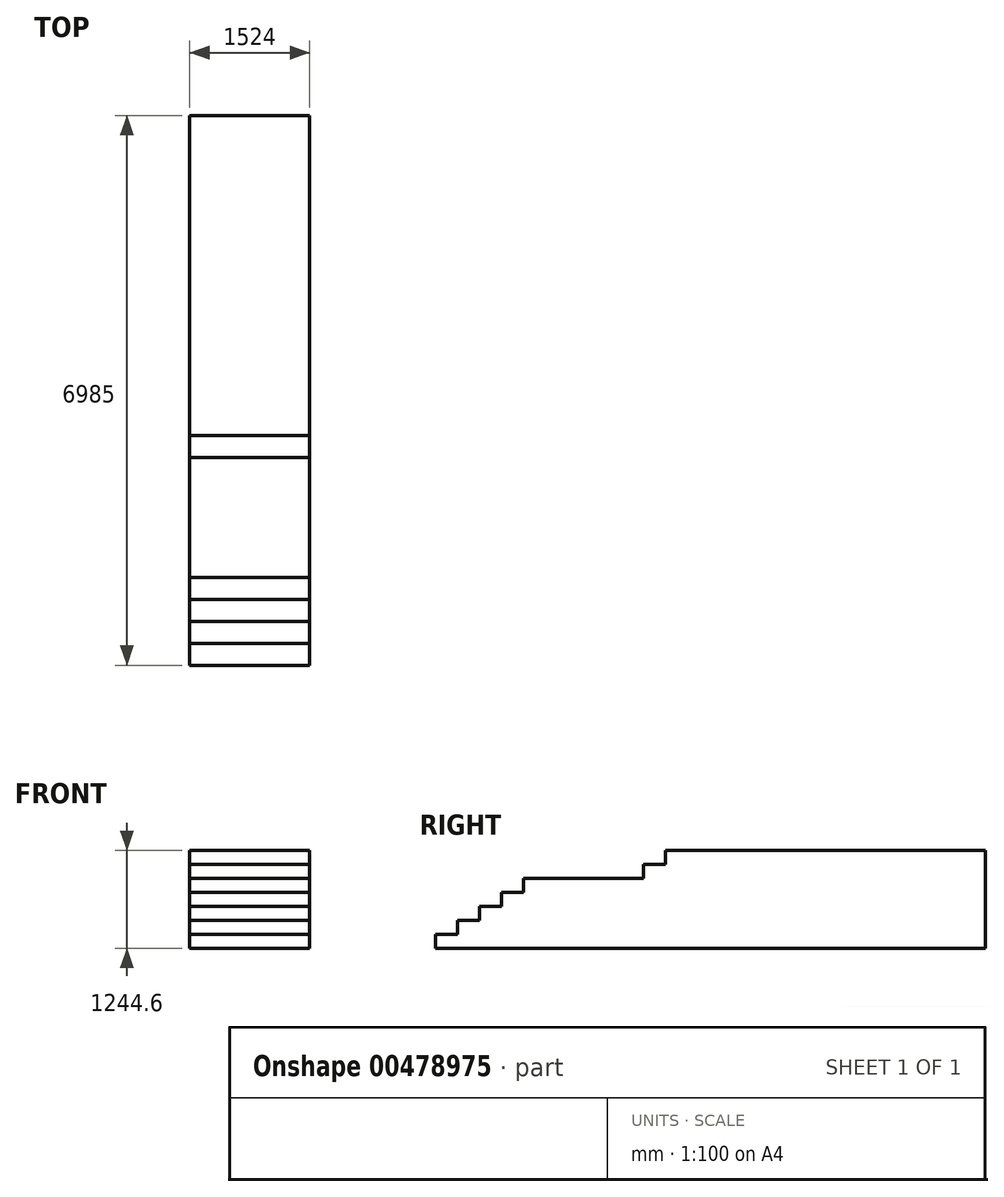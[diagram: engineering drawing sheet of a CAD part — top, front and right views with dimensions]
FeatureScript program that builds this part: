
annotation { "Feature Type Name" : "Feature", "Feature Type Description" : "" }
export const myFeature = defineFeature(function(context is Context, id is Id, definition is map)
    precondition{}
    {
        {
            var Q0;
            Q0=qCreatedBy(makeId("Top.planeOp"),FACE);
            var sketch = newSketch(context, id + "F0", { "sketchPlane" : qUnion([Q0])});
            skLineSegment(sketch, "E0.bottom", {"start": v(-763, 4345.35) * mm, "end": v(761, 4345.35) * mm});
            skLineSegment(sketch, "E0.top", {"start": v(-763, -2639.65) * mm, "end": v(761, -2639.65) * mm});
            skLineSegment(sketch, "E0.left", {"start": v(-763, 4345.35) * mm, "end": v(-763, -2639.65) * mm});
            skLineSegment(sketch, "E0.right", {"start": v(761, 4345.35) * mm, "end": v(761, -2639.65) * mm});
            skSolve(sketch);
        }
        {
            var Q0;
            Q0 = qSketchRegion(id + "F0", true);
            extrude(context, id + "F1", {"entities" : qUnion([Q0]), "depth" : 177.8 * mm});
        }
        {
            var Q0;
            Q0=makeQuery(id+"F1.opExtrude","CAP_FACE",FACE,{"disambiguationData":[OSD([sQuery(id+"F0.wireOp",EDGE,"E0.bottom"),sQuery(id+"F0.wireOp",EDGE,"E0.top"),sQuery(id+"F0.wireOp",EDGE,"E0.left"),sQuery(id+"F0.wireOp",EDGE,"E0.right")])],"isStart":false});
            var sketch = newSketch(context, id + "F2", { "sketchPlane" : qUnion([Q0])});
            skPoint(sketch, "E1", {"position": v(-763, -2360.25) * mm});
            skPoint(sketch, "E2", {"position": v(761, -2360.25) * mm});
            skLineSegment(sketch, "E3.bottom", {"start": v(-763, -2360.25) * mm, "end": v(761, -2360.25) * mm});
            skLineSegment(sketch, "E3.top", {"start": v(-763, 4345.35) * mm, "end": v(761, 4345.35) * mm});
            skLineSegment(sketch, "E3.left", {"start": v(-763, -2360.25) * mm, "end": v(-763, 4345.35) * mm});
            skLineSegment(sketch, "E3.right", {"start": v(761, -2360.25) * mm, "end": v(761, 4345.35) * mm});
            skSolve(sketch);
        }
        {
            var Q0;
            Q0=makeQuery(id+"F2.imprint","IMPRINT",FACE,{"disambiguationData":[TD([[makeQuery(id+"F2.imprint","IMPRINT",EDGE,{"derivedFrom":sQuery(id+"F2.wireOp",EDGE,"E3.bottom")}),1.0]])]});
            extrude(context, id + "F3", {"entities" : qUnion([Q0]), "operationType" : NewBodyOperationType.ADD, "depth" : 177.8 * mm});
        }
        {
            var Q0;
            Q0=makeQuery(id+"F3.opExtrude","CAP_FACE",FACE,{"disambiguationData":[OSD([sQuery(id+"F2.wireOp",EDGE,"E3.bottom"),sQuery(id+"F2.wireOp",EDGE,"E3.top"),sQuery(id+"F2.wireOp",EDGE,"E3.left"),sQuery(id+"F2.wireOp",EDGE,"E3.right")])],"isStart":false});
            var sketch = newSketch(context, id + "F4", { "sketchPlane" : qUnion([Q0])});
            skPoint(sketch, "E4", {"position": v(-763, -2080.85) * mm});
            skPoint(sketch, "E5", {"position": v(761, -2080.85) * mm});
            skLineSegment(sketch, "E6.bottom", {"start": v(-763, -2080.85) * mm, "end": v(761, -2080.85) * mm});
            skLineSegment(sketch, "E6.top", {"start": v(-763, 4345.35) * mm, "end": v(761, 4345.35) * mm});
            skLineSegment(sketch, "E6.left", {"start": v(-763, -2080.85) * mm, "end": v(-763, 4345.35) * mm});
            skLineSegment(sketch, "E6.right", {"start": v(761, -2080.85) * mm, "end": v(761, 4345.35) * mm});
            skSolve(sketch);
        }
        {
            var Q0;
            Q0 = qSketchRegion(id + "F4", true);
            var Q1;
            Q1=makeQuery(id+"F4.imprint","IMPRINT",FACE,{"disambiguationData":[TD([[makeQuery(id+"F4.imprint","IMPRINT",EDGE,{"derivedFrom":sQuery(id+"F4.wireOp",EDGE,"E6.bottom")}),1.0]])]});
            extrude(context, id + "F5", {"entities" : qUnion([Q0, Q1]), "operationType" : NewBodyOperationType.ADD, "depth" : 177.8 * mm});
        }
        {
            var Q0;
            Q0=makeQuery(id+"F5.opExtrude","CAP_FACE",FACE,{"disambiguationData":[OSD([sQuery(id+"F4.wireOp",EDGE,"E6.bottom"),sQuery(id+"F4.wireOp",EDGE,"E6.top"),sQuery(id+"F4.wireOp",EDGE,"E6.left"),sQuery(id+"F4.wireOp",EDGE,"E6.right")])],"isStart":false});
            var sketch = newSketch(context, id + "F6", { "sketchPlane" : qUnion([Q0])});
            skPoint(sketch, "E7", {"position": v(-763, -1801.45) * mm});
            skPoint(sketch, "E8", {"position": v(761, -1801.45) * mm});
            skLineSegment(sketch, "E9.bottom", {"start": v(-763, -1801.45) * mm, "end": v(761, -1801.45) * mm});
            skLineSegment(sketch, "E9.top", {"start": v(-763, 4345.35) * mm, "end": v(761, 4345.35) * mm});
            skLineSegment(sketch, "E9.left", {"start": v(-763, -1801.45) * mm, "end": v(-763, 4345.35) * mm});
            skLineSegment(sketch, "E9.right", {"start": v(761, -1801.45) * mm, "end": v(761, 4345.35) * mm});
            skSolve(sketch);
        }
        {
            var Q0;
            Q0 = qSketchRegion(id + "F6", true);
            extrude(context, id + "F7", {"entities" : qUnion([Q0]), "operationType" : NewBodyOperationType.ADD, "depth" : 177.8 * mm});
        }
        {
            var Q0;
            Q0=makeQuery(id+"F7.opExtrude","CAP_FACE",FACE,{"disambiguationData":[OSD([sQuery(id+"F6.wireOp",EDGE,"E9.bottom"),sQuery(id+"F6.wireOp",EDGE,"E9.top"),sQuery(id+"F6.wireOp",EDGE,"E9.left"),sQuery(id+"F6.wireOp",EDGE,"E9.right")])],"isStart":false});
            var sketch = newSketch(context, id + "F8", { "sketchPlane" : qUnion([Q0])});
            skPoint(sketch, "E10", {"position": v(-763, -1522.05) * mm});
            skPoint(sketch, "E11", {"position": v(761, -1522.05) * mm});
            skLineSegment(sketch, "E12.bottom", {"start": v(-763, -1522.05) * mm, "end": v(761, -1522.05) * mm});
            skLineSegment(sketch, "E12.top", {"start": v(-763, 4345.35) * mm, "end": v(761, 4345.35) * mm});
            skLineSegment(sketch, "E12.left", {"start": v(-763, -1522.05) * mm, "end": v(-763, 4345.35) * mm});
            skLineSegment(sketch, "E12.right", {"start": v(761, -1522.05) * mm, "end": v(761, 4345.35) * mm});
            skSolve(sketch);
        }
        {
            var Q0;
            Q0 = qSketchRegion(id + "F8", true);
            var Q1;
            Q1=makeQuery(id+"F8.imprint","IMPRINT",FACE,{"disambiguationData":[TD([[makeQuery(id+"F8.imprint","IMPRINT",EDGE,{"derivedFrom":sQuery(id+"F8.wireOp",EDGE,"E12.bottom")}),1.0]])]});
            extrude(context, id + "F9", {"entities" : qUnion([Q0, Q1]), "operationType" : NewBodyOperationType.ADD, "depth" : 177.8 * mm});
        }
        {
            var Q0;
            Q0=makeQuery(id+"F9.opExtrude","CAP_FACE",FACE,{"disambiguationData":[OSD([sQuery(id+"F8.wireOp",EDGE,"E12.bottom"),sQuery(id+"F8.wireOp",EDGE,"E12.top"),sQuery(id+"F8.wireOp",EDGE,"E12.left"),sQuery(id+"F8.wireOp",EDGE,"E12.right")])],"isStart":false});
            var sketch = newSketch(context, id + "F10", { "sketchPlane" : qUnion([Q0])});
            skPoint(sketch, "E13", {"position": v(-763, 1.95) * mm});
            skPoint(sketch, "E14", {"position": v(761, 1.95) * mm});
            skLineSegment(sketch, "E15.bottom", {"start": v(-763, 1.95) * mm, "end": v(761, 1.95) * mm});
            skLineSegment(sketch, "E15.top", {"start": v(-763, 4345.35) * mm, "end": v(761, 4345.35) * mm});
            skLineSegment(sketch, "E15.left", {"start": v(-763, 1.95) * mm, "end": v(-763, 4345.35) * mm});
            skLineSegment(sketch, "E15.right", {"start": v(761, 1.95) * mm, "end": v(761, 4345.35) * mm});
            skSolve(sketch);
        }
        {
            var Q0;
            Q0 = qSketchRegion(id + "F10", true);
            var Q1;
            Q1=makeQuery(id+"F10.imprint","IMPRINT",FACE,{"disambiguationData":[TD([[makeQuery(id+"F10.imprint","IMPRINT",EDGE,{"derivedFrom":sQuery(id+"F10.wireOp",EDGE,"E15.bottom")}),1.0]])]});
            extrude(context, id + "F11", {"entities" : qUnion([Q0, Q1]), "operationType" : NewBodyOperationType.ADD, "depth" : 177.8 * mm});
        }
        {
            var Q0;
            Q0=makeQuery(id+"F11.opExtrude","CAP_FACE",FACE,{"disambiguationData":[OSD([sQuery(id+"F10.wireOp",EDGE,"E15.bottom"),sQuery(id+"F10.wireOp",EDGE,"E15.top"),sQuery(id+"F10.wireOp",EDGE,"E15.left"),sQuery(id+"F10.wireOp",EDGE,"E15.right")])],"isStart":false});
            var sketch = newSketch(context, id + "F12", { "sketchPlane" : qUnion([Q0])});
            skPoint(sketch, "E16", {"position": v(-763, 281.35) * mm});
            skPoint(sketch, "E17", {"position": v(761, 281.35) * mm});
            skLineSegment(sketch, "E18.bottom", {"start": v(-763, 281.35) * mm, "end": v(761, 281.35) * mm});
            skLineSegment(sketch, "E18.top", {"start": v(-763, 4345.35) * mm, "end": v(761, 4345.35) * mm});
            skLineSegment(sketch, "E18.left", {"start": v(-763, 281.35) * mm, "end": v(-763, 4345.35) * mm});
            skLineSegment(sketch, "E18.right", {"start": v(761, 281.35) * mm, "end": v(761, 4345.35) * mm});
            skSolve(sketch);
        }
        {
            var Q0;
            Q0=makeQuery(id+"F12.imprint","IMPRINT",FACE,{"disambiguationData":[TD([[makeQuery(id+"F12.imprint","IMPRINT",EDGE,{"derivedFrom":sQuery(id+"F12.wireOp",EDGE,"E18.bottom")}),1.0]])]});
            extrude(context, id + "F13", {"entities" : qUnion([Q0]), "operationType" : NewBodyOperationType.ADD, "depth" : 177.8 * mm});
        }
    });
